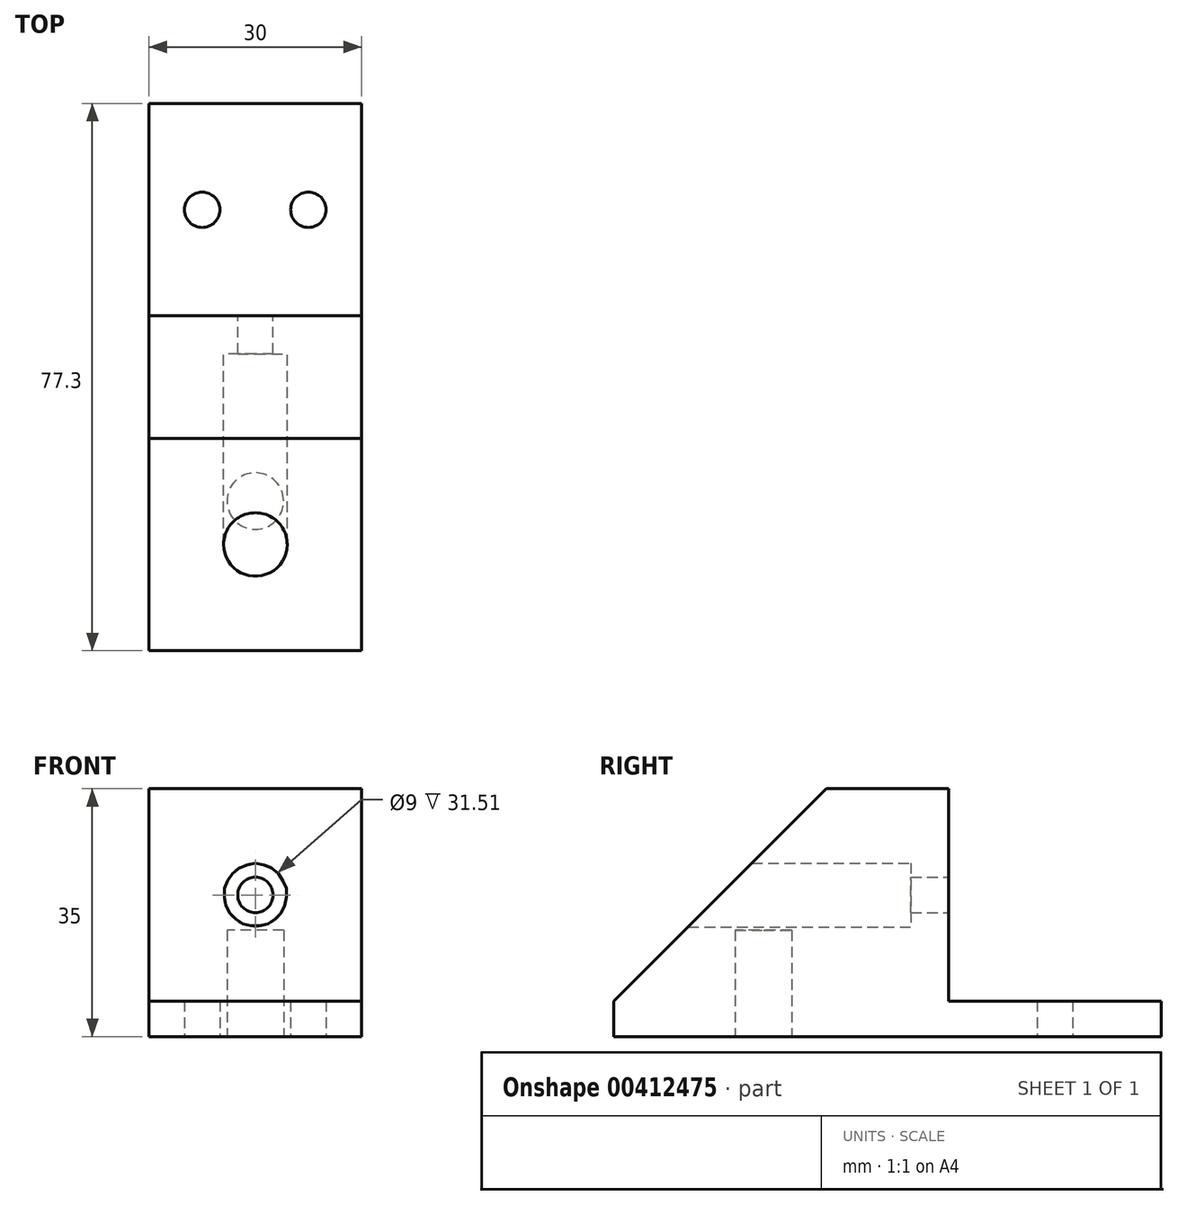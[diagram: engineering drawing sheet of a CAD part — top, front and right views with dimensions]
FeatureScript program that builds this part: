
annotation { "Feature Type Name" : "Feature", "Feature Type Description" : "" }
export const myFeature = defineFeature(function(context is Context, id is Id, definition is map)
    precondition{}
    {
        {
            var Q0;
            Q0=qCreatedBy(makeId("Top.planeOp"),FACE);
            var sketch = newSketch(context, id + "F0", { "sketchPlane" : qUnion([Q0])});
            skLineSegment(sketch, "E0.bottom", {"start": v(14.98, 39) * mm, "end": v(-15.02, 39) * mm});
            skLineSegment(sketch, "E0.top", {"start": v(14.98, -38.3) * mm, "end": v(-15.02, -38.3) * mm});
            skLineSegment(sketch, "E0.left", {"start": v(14.98, 39) * mm, "end": v(14.98, -38.3) * mm});
            skLineSegment(sketch, "E0.right", {"start": v(-15.02, 39) * mm, "end": v(-15.02, -38.3) * mm});
            skPoint(sketch, "E0.middle", {"position": v(-0.02, 0.35) * mm});
            skLineSegment(sketch, "E1", {"start": v(-15.02, 9) * mm, "end": v(14.98, 9) * mm});
            skLineSegment(sketch, "E2.0", {"start": v(-15.02, 4) * mm, "end": v(14.98, 4) * mm});
            skPoint(sketch, "E3", {"position": v(-0.02, -17.15) * mm});
            skCircle(sketch, "E4", {"center": v(-0.02, -17.15) * mm, "radius": 4 * mm});
            skCircle(sketch, "E5", {"center": v(-7.52, 24) * mm, "radius": 2.5 * mm});
            skCircle(sketch, "E6", {"center": v(7.48, 24) * mm, "radius": 2.5 * mm});
            skSolve(sketch);
        }
        {
            var Q0;
            {var subQ2=sQuery(id+"F0.wireOp",EDGE,"E0.bottom");Q0=makeQuery(id+"F0.imprint","IMPRINT",FACE,{"disambiguationData":[TD([[makeQuery(id+"F0.imprint","IMPRINT",EDGE,{"derivedFrom":subQ2}),1.0]])]});}
            var Q1;
            {var subQ0=sQuery(id+"F0.wireOp",EDGE,"E1");Q1=makeQuery(id+"F0.imprint","IMPRINT",FACE,{"disambiguationData":[TD([[makeQuery(id+"F0.imprint","IMPRINT",EDGE,{"derivedFrom":subQ0}),-1.0]])]});}
            var Q2;
            {var subQ1=sQuery(id+"F0.wireOp",EDGE,"E0.top");Q2=makeQuery(id+"F0.imprint","IMPRINT",FACE,{"disambiguationData":[TD([[makeQuery(id+"F0.imprint","IMPRINT",EDGE,{"derivedFrom":subQ1}),-1.0]])]});}
            var Q3;
            Q3=makeQuery(id+"F0.imprint","IMPRINT",FACE,{"disambiguationData":[TD([[makeQuery(id+"F0.imprint","IMPRINT",EDGE,{"derivedFrom":sQuery(id+"F0.wireOp",EDGE,"E4")}),1.0]])]});
            extrude(context, id + "F1", {"entities" : qUnion([Q0, Q1, Q2, Q3]), "depth" : 5 * mm});
        }
        {
            var Q0;
            {var subQ0=sQuery(id+"F0.wireOp",EDGE,"E1");Q0=makeQuery(id+"F0.imprint","IMPRINT",FACE,{"disambiguationData":[TD([[makeQuery(id+"F0.imprint","IMPRINT",EDGE,{"derivedFrom":subQ0}),-1.0]])]});}
            var Q1;
            {var subQ1=sQuery(id+"F0.wireOp",EDGE,"E0.top");Q1=makeQuery(id+"F0.imprint","IMPRINT",FACE,{"disambiguationData":[TD([[makeQuery(id+"F0.imprint","IMPRINT",EDGE,{"derivedFrom":subQ1}),-1.0]])]});}
            var Q2;
            Q2=makeQuery(id+"F0.imprint","IMPRINT",FACE,{"disambiguationData":[TD([[makeQuery(id+"F0.imprint","IMPRINT",EDGE,{"derivedFrom":sQuery(id+"F0.wireOp",EDGE,"E4")}),1.0]])]});
            extrude(context, id + "F2", {"entities" : qUnion([Q0, Q1, Q2]), "operationType" : NewBodyOperationType.ADD, "depth" : 35 * mm});
        }
        {
            var Q0;
            Q0=makeQuery(id+"F0.imprint","IMPRINT",FACE,{"disambiguationData":[TD([[makeQuery(id+"F0.imprint","IMPRINT",EDGE,{"derivedFrom":sQuery(id+"F0.wireOp",EDGE,"E4")}),1.0]])]});
            extrude(context, id + "F3", {"entities" : qUnion([Q0]), "operationType" : NewBodyOperationType.REMOVE, "depth" : 15 * mm});
        }
        {
            var Q0;
            Q0=makeQuery(id+"F2.opExtrude","CAP_EDGE",EDGE,{"disambiguationData":[OSD([sQuery(id+"F0.wireOp",EDGE,"E0.top")])],"isStart":false});
            chamfer(context, id + "F4", {"entities" : qUnion([Q0]), "width" : 30 * mm, "tangentPropagation" : true});
        }
        {
            var Q0;
            Q0=qCreatedBy(makeId("Front.planeOp"),FACE);
            var sketch = newSketch(context, id + "F5", { "sketchPlane" : qUnion([Q0])});
            skPoint(sketch, "E7", {"position": v(0, 20) * mm});
            skCircle(sketch, "E8", {"center": v(0, 20) * mm, "radius": 2.5 * mm});
            skCircle(sketch, "E9.0", {"center": v(0, 20) * mm, "radius": 4.5 * mm});
            skSolve(sketch);
        }
        {
            var Q0;
            Q0=makeQuery(id+"F5.imprint","IMPRINT",FACE,{"disambiguationData":[TD([[makeQuery(id+"F5.imprint","IMPRINT",EDGE,{"derivedFrom":sQuery(id+"F5.wireOp",EDGE,"E8")}),1.0]])]});
            extrude(context, id + "F6", {"entities" : qUnion([Q0]), "operationType" : NewBodyOperationType.REMOVE, "depth" : 35 * mm, "hasSecondDirection" : true, "secondDirectionOppositeDirection" : true, "secondDirectionDepth" : 9 * mm});
        }
        {
            var Q0;
            Q0=makeQuery(id+"F5.imprint","IMPRINT",FACE,{"disambiguationData":[TD([[makeQuery(id+"F5.imprint","IMPRINT",EDGE,{"derivedFrom":sQuery(id+"F5.wireOp",EDGE,"E8")}),-1.0]])]});
            extrude(context, id + "F7", {"entities" : qUnion([Q0]), "operationType" : NewBodyOperationType.REMOVE, "depth" : 35 * mm, "hasSecondDirection" : true, "secondDirectionOppositeDirection" : true, "secondDirectionDepth" : 3.65 * mm});
        }
    });
